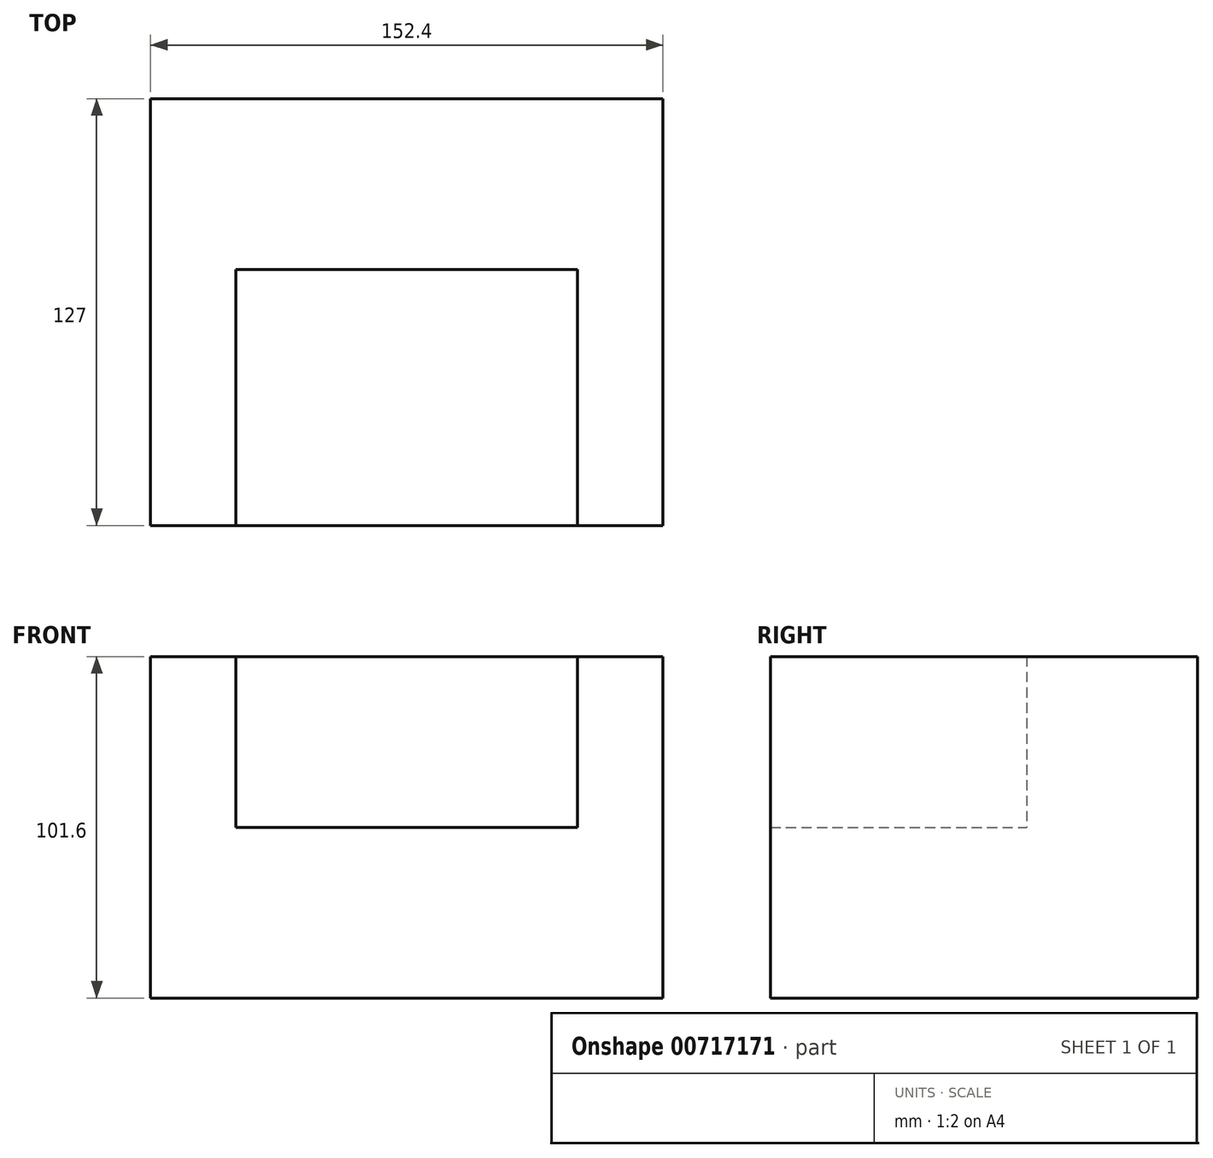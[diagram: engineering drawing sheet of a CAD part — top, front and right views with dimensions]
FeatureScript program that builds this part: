
annotation { "Feature Type Name" : "Feature", "Feature Type Description" : "" }
export const myFeature = defineFeature(function(context is Context, id is Id, definition is map)
    precondition{}
    {
        {
            var Q0;
            Q0=qCreatedBy(makeId("Front.planeOp"),FACE);
            var sketch = newSketch(context, id + "F0", { "sketchPlane" : qUnion([Q0])});
            skLineSegment(sketch, "E0", {"start": v(-68.4, -47.7) * mm, "end": v(84, -47.7) * mm});
            skLineSegment(sketch, "E1", {"start": v(84, -47.7) * mm, "end": v(84, 53.9) * mm});
            skLineSegment(sketch, "E2", {"start": v(84, 53.9) * mm, "end": v(58.6, 53.9) * mm});
            skLineSegment(sketch, "E3", {"start": v(58.6, 53.9) * mm, "end": v(58.6, 3.1) * mm});
            skLineSegment(sketch, "E4", {"start": v(58.6, 3.1) * mm, "end": v(-43, 3.1) * mm});
            skLineSegment(sketch, "E5", {"start": v(-43, 3.1) * mm, "end": v(-43, 53.9) * mm});
            skLineSegment(sketch, "E6", {"start": v(-43, 53.9) * mm, "end": v(-68.4, 53.9) * mm});
            skLineSegment(sketch, "E7", {"start": v(-68.4, 53.9) * mm, "end": v(-68.4, -47.7) * mm});
            skSolve(sketch);
        }
        {
            var Q0;
            Q0=makeQuery(id+"F0.imprint","IMPRINT",FACE,{"disambiguationData":[TD([[makeQuery(id+"F0.imprint","IMPRINT",EDGE,{"derivedFrom":sQuery(id+"F0.wireOp",EDGE,"E0")}),1.0]])]});
            extrude(context, id + "F1", {"entities" : qUnion([Q0]), "depth" : 76.2 * mm, "offsetDistance" : 25.4 * mm});
        }
        {
            var Q0;
            Q0=makeQuery(id+"F1.opExtrude","CAP_FACE",FACE,{"disambiguationData":[OSD([sQuery(id+"F0.wireOp",EDGE,"E0"),sQuery(id+"F0.wireOp",EDGE,"E1"),sQuery(id+"F0.wireOp",EDGE,"E2"),sQuery(id+"F0.wireOp",EDGE,"E3"),sQuery(id+"F0.wireOp",EDGE,"E4"),sQuery(id+"F0.wireOp",EDGE,"E5"),sQuery(id+"F0.wireOp",EDGE,"E6"),sQuery(id+"F0.wireOp",EDGE,"E7")])],"isStart":true});
            var sketch = newSketch(context, id + "F2", { "sketchPlane" : qUnion([Q0])});
            skLineSegment(sketch, "E8.bottom", {"start": v(-84, 53.9) * mm, "end": v(68.4, 53.9) * mm});
            skLineSegment(sketch, "E8.top", {"start": v(-84, -47.7) * mm, "end": v(68.4, -47.7) * mm});
            skLineSegment(sketch, "E8.left", {"start": v(-84, 53.9) * mm, "end": v(-84, -47.7) * mm});
            skLineSegment(sketch, "E8.right", {"start": v(68.4, 53.9) * mm, "end": v(68.4, -47.7) * mm});
            skSolve(sketch);
        }
        {
            var Q0;
            {var subQ1=makeQuery(id+"F1.opExtrude","CAP_EDGE",EDGE,{"disambiguationData":[OSD([sQuery(id+"F0.wireOp",EDGE,"E3")])],"isStart":true});Q0=makeQuery(id+"F2.imprint","IMPRINT",FACE,{"disambiguationData":[TD([[makeQuery(id+"F2.imprint","IMPRINT",EDGE,{"derivedFrom":subQ1}),1.0]])]});}
            var Q1;
            Q1=makeQuery(id+"F2.imprint","IMPRINT",FACE,{"disambiguationData":[TD([[makeQuery(id+"F2.imprint","IMPRINT",EDGE,{"derivedFrom":sQuery(id+"F2.wireOp",EDGE,"E8.top")}),-1.0]])]});
            extrude(context, id + "F3", {"entities" : qUnion([Q0, Q1]), "operationType" : NewBodyOperationType.ADD, "depth" : 50.8 * mm, "offsetDistance" : 25.4 * mm});
        }
    });
